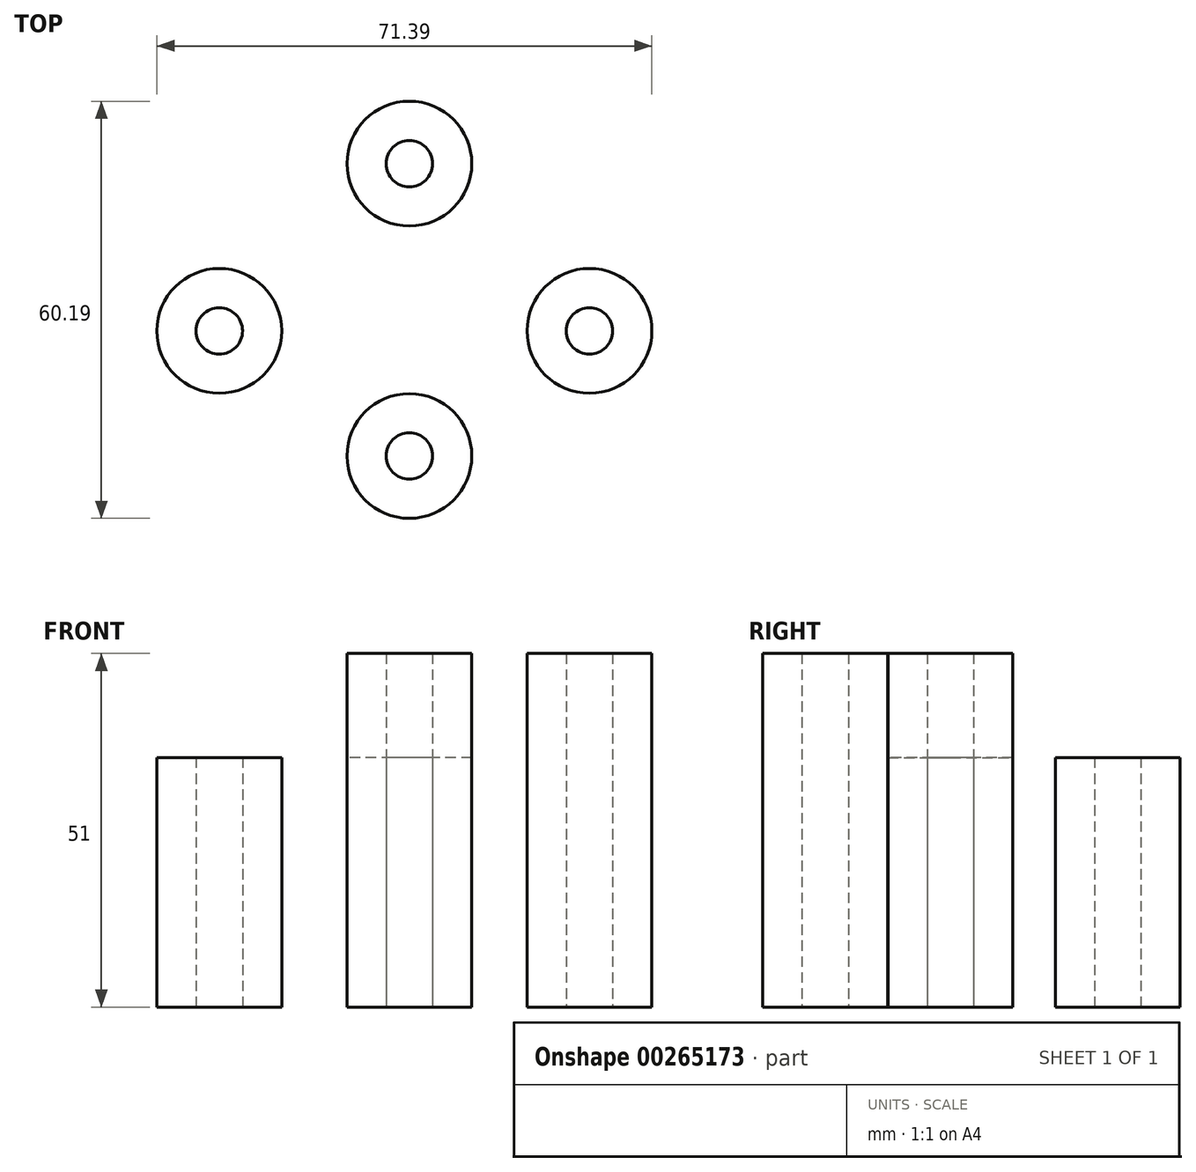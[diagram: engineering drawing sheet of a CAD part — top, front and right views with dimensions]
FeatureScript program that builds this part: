
annotation { "Feature Type Name" : "Feature", "Feature Type Description" : "" }
export const myFeature = defineFeature(function(context is Context, id is Id, definition is map)
    precondition{}
    {
        {
            var Q0;
            Q0=qCreatedBy(makeId("Top.planeOp"),FACE);
            var sketch = newSketch(context, id + "F0", { "sketchPlane" : qUnion([Q0])});
            skCircle(sketch, "E0", {"center": v(25.98, 0) * mm, "radius": 9 * mm});
            skCircle(sketch, "E1", {"center": v(25.98, 0) * mm, "radius": 3.35 * mm});
            skCircle(sketch, "E2", {"center": v(-27.41, 0) * mm, "radius": 3.35 * mm});
            skCircle(sketch, "E3", {"center": v(-27.41, 0) * mm, "radius": 9 * mm});
            skCircle(sketch, "E4", {"center": v(0, 24.14) * mm, "radius": 3.35 * mm});
            skCircle(sketch, "E5", {"center": v(0, 24.14) * mm, "radius": 9 * mm});
            skCircle(sketch, "E6", {"center": v(0, -18.05) * mm, "radius": 9 * mm});
            skCircle(sketch, "E7", {"center": v(0, -18.05) * mm, "radius": 3.35 * mm});
            skSolve(sketch);
        }
        {
            var Q0;
            Q0=makeQuery(id+"F0.imprint","IMPRINT",FACE,{"disambiguationData":[TD([[makeQuery(id+"F0.imprint","IMPRINT",EDGE,{"derivedFrom":sQuery(id+"F0.wireOp",EDGE,"E2")}),-1.0]])]});
            var Q1;
            Q1=makeQuery(id+"F0.imprint","IMPRINT",FACE,{"disambiguationData":[TD([[makeQuery(id+"F0.imprint","IMPRINT",EDGE,{"derivedFrom":sQuery(id+"F0.wireOp",EDGE,"E4")}),-1.0]])]});
            extrude(context, id + "F1", {"entities" : qUnion([Q0, Q1]), "depth" : 36 * mm});
        }
        {
            var Q0;
            Q0=makeQuery(id+"F0.imprint","IMPRINT",FACE,{"disambiguationData":[TD([[makeQuery(id+"F0.imprint","IMPRINT",EDGE,{"derivedFrom":sQuery(id+"F0.wireOp",EDGE,"E6")}),1.0]])]});
            var Q1;
            Q1=makeQuery(id+"F0.imprint","IMPRINT",FACE,{"disambiguationData":[TD([[makeQuery(id+"F0.imprint","IMPRINT",EDGE,{"derivedFrom":sQuery(id+"F0.wireOp",EDGE,"E0")}),1.0]])]});
            extrude(context, id + "F2", {"entities" : qUnion([Q0, Q1]), "depth" : 51 * mm});
        }
    });
